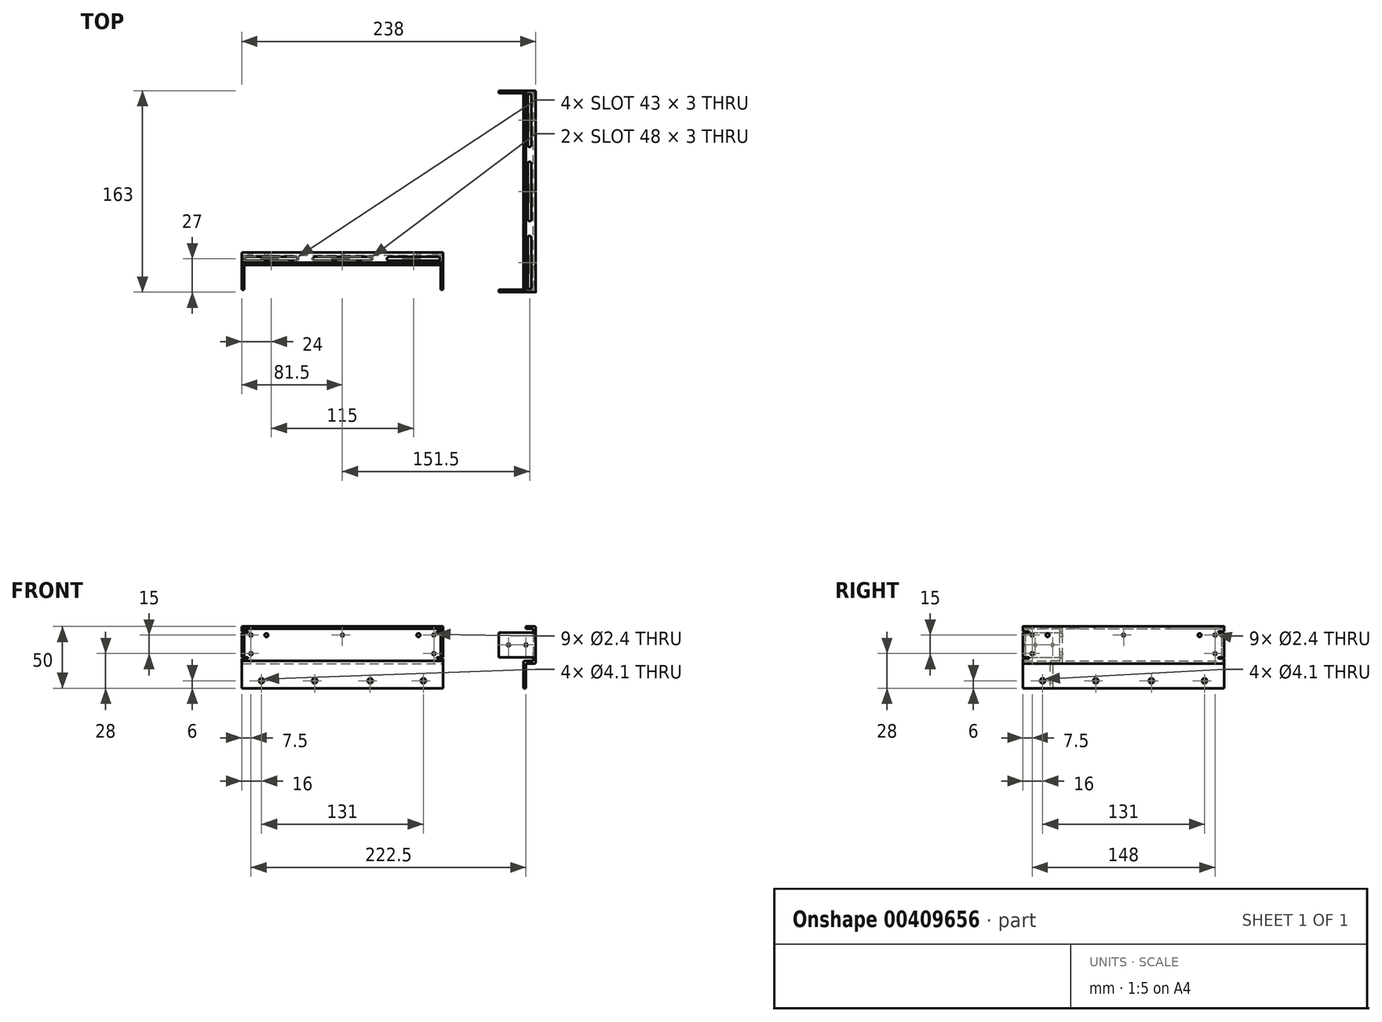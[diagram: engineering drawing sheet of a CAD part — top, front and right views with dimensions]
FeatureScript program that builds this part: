
annotation { "Feature Type Name" : "Feature", "Feature Type Description" : "" }
export const myFeature = defineFeature(function(context is Context, id is Id, definition is map)
    precondition{}
    {
        {
            var Q0;
            Q0=qCreatedBy(makeId("Front.planeOp"),FACE);
            var sketch = newSketch(context, id + "F0", { "sketchPlane" : qUnion([Q0])});
            skLineSegment(sketch, "E0", {"start": v(-20, 60) * mm, "end": v(-12, 60) * mm});
            skLineSegment(sketch, "E1", {"start": v(-12, 60) * mm, "end": v(-12, 58) * mm});
            skLineSegment(sketch, "E2", {"start": v(-12, 58) * mm, "end": v(-18, 58) * mm});
            skLineSegment(sketch, "E3", {"start": v(-18, 58) * mm, "end": v(-18, 32) * mm});
            skLineSegment(sketch, "E4", {"start": v(-20, 30) * mm, "end": v(-20, 60) * mm});
            skLineSegment(sketch, "E5.bottom", {"start": v(-18, 32) * mm, "end": v(-10, 32) * mm});
            skLineSegment(sketch, "E5.top", {"start": v(-20, 30) * mm, "end": v(-12, 30) * mm});
            skLineSegment(sketch, "E6.top", {"start": v(-10, 10) * mm, "end": v(-12, 10) * mm});
            skLineSegment(sketch, "E6.left", {"start": v(-10, 32) * mm, "end": v(-10, 10) * mm});
            skLineSegment(sketch, "E6.right", {"start": v(-12, 30) * mm, "end": v(-12, 10) * mm});
            skSolve(sketch);
        }
        {
            var Q0;
            Q0=qSketchRegion(id+"F0",true);
            extrude(context, id + "F1", {"entities" : qUnion([Q0]), "depth" : 163 * mm});
        }
        {
            var Q0;
            Q0=makeQuery(id+"F1.opExtrude","SWEPT_FACE",FACE,{"disambiguationData":[OSD([sQuery(id+"F0.wireOp",EDGE,"E3")])]});
            var sketch = newSketch(context, id + "F2", { "sketchPlane" : qUnion([Q0])});
            skLineSegment(sketch, "E7.bottom", {"start": v(0, 35) * mm, "end": v(-2, 35) * mm});
            skLineSegment(sketch, "E7.top", {"start": v(0, 55) * mm, "end": v(-2, 55) * mm});
            skLineSegment(sketch, "E7.left", {"start": v(0, 35) * mm, "end": v(0, 55) * mm});
            skLineSegment(sketch, "E7.right", {"start": v(-2, 35) * mm, "end": v(-2, 55) * mm});
            skLineSegment(sketch, "E8.bottom", {"start": v(-163, 55) * mm, "end": v(-161, 55) * mm});
            skLineSegment(sketch, "E8.top", {"start": v(-163, 35) * mm, "end": v(-161, 35) * mm});
            skLineSegment(sketch, "E8.left", {"start": v(-163, 55) * mm, "end": v(-163, 35) * mm});
            skLineSegment(sketch, "E8.right", {"start": v(-161, 55) * mm, "end": v(-161, 35) * mm});
            skSolve(sketch);
        }
        {
            var Q0;
            Q0=qSketchRegion(id+"F2",true);
            extrude(context, id + "F3", {"entities" : qUnion([Q0]), "operationType" : NewBodyOperationType.ADD, "depth" : 28 * mm});
        }
        {
            var Q0;
            Q0=makeQuery(id+"F1.opExtrude","SWEPT_FACE",FACE,{"disambiguationData":[OSD([sQuery(id+"F0.wireOp",EDGE,"E0")])]});
            var sketch = newSketch(context, id + "F4", { "sketchPlane" : qUnion([Q0])});
            skLineSegment(sketch, "E9", {"start": v(30.39, -75) * mm, "end": v(87.94, -75) * mm, "construction": true});
            skLineSegment(sketch, "E10", {"start": v(27.83, -140) * mm, "end": v(81.96, -140) * mm, "construction": true});
            skLineSegment(sketch, "E11", {"start": v(28.86, -163) * mm, "end": v(81.02, -163) * mm, "construction": true});
            skPoint(sketch, "E12", {"position": v(-41.07, -12.5) * mm});
            skPoint(sketch, "E13", {"position": v(-41.07, -62.5) * mm});
            skPoint(sketch, "E14", {"position": v(-41.07, -87.5) * mm});
            skPoint(sketch, "E15", {"position": v(-41.07, -127.5) * mm});
            skPoint(sketch, "E16", {"position": v(-41.07, -145) * mm});
            skPoint(sketch, "E17", {"position": v(-41.07, -158) * mm});
            skLineSegment(sketch, "E18", {"start": v(-168.81, -81.5) * mm, "end": v(221.3, -81.5) * mm, "construction": true});
            skLineSegment(sketch, "E19.bottom", {"start": v(-13.5, -104) * mm, "end": v(-16.5, -104) * mm, "construction": true});
            skLineSegment(sketch, "E19.top", {"start": v(-13.5, -59) * mm, "end": v(-16.5, -59) * mm, "construction": true});
            skLineSegment(sketch, "E19.left", {"start": v(-13.5, -104) * mm, "end": v(-13.5, -59) * mm});
            skLineSegment(sketch, "E19.right", {"start": v(-16.5, -104) * mm, "end": v(-16.5, -59) * mm});
            skPoint(sketch, "E19.middle", {"position": v(-15, -81.5) * mm});
            skArc(sketch, "E20", {"start": v(-13.5, -59) * mm, "mid": v(-15, -57.5) * mm, "end": v(-16.5, -59) * mm});
            skArc(sketch, "E21", {"start": v(-16.5, -104) * mm, "mid": v(-15, -105.5) * mm, "end": v(-13.5, -104) * mm});
            skLineSegment(sketch, "E22.bottom", {"start": v(-13.5, -44) * mm, "end": v(-16.5, -44) * mm, "construction": true});
            skLineSegment(sketch, "E22.top", {"start": v(-13.5, -4) * mm, "end": v(-16.5, -4) * mm, "construction": true});
            skLineSegment(sketch, "E22.left", {"start": v(-13.5, -44) * mm, "end": v(-13.5, -4) * mm});
            skLineSegment(sketch, "E22.right", {"start": v(-16.5, -44) * mm, "end": v(-16.5, -4) * mm});
            skPoint(sketch, "E22.middle", {"position": v(-15, -24) * mm});
            skArc(sketch, "E23", {"start": v(-13.5, -4) * mm, "mid": v(-15, -2.5) * mm, "end": v(-16.5, -4) * mm});
            skArc(sketch, "E24", {"start": v(-16.5, -44) * mm, "mid": v(-15, -45.5) * mm, "end": v(-13.5, -44) * mm});
            skLineSegment(sketch, "E25.MirrorCS", {"start": v(-13.5, -159) * mm, "end": v(-16.5, -159) * mm, "construction": true});
            skLineSegment(sketch, "E26.MirrorCS", {"start": v(-13.5, -119) * mm, "end": v(-16.5, -119) * mm, "construction": true});
            skArc(sketch, "E27.MirrorCS", {"start": v(-16.5, -119) * mm, "mid": v(-15, -117.5) * mm, "end": v(-13.5, -119) * mm});
            skArc(sketch, "E28.MirrorCS", {"start": v(-13.5, -159) * mm, "mid": v(-15, -160.5) * mm, "end": v(-16.5, -159) * mm});
            skPoint(sketch, "E29.MirrorP", {"position": v(-15, -139) * mm});
            skLineSegment(sketch, "E30.MirrorCS", {"start": v(-13.5, -119) * mm, "end": v(-13.5, -159) * mm});
            skLineSegment(sketch, "E31.MirrorCS", {"start": v(-16.5, -119) * mm, "end": v(-16.5, -159) * mm});
            skSolve(sketch);
        }
        {
            var Q0;
            Q0=qSketchRegion(id+"F4",true);
            extrude(context, id + "F5", {"entities" : qUnion([Q0]), "operationType" : NewBodyOperationType.REMOVE, "oppositeDirection" : true, "depth" : 2 * mm});
        }
        {
            var Q0;
            Q0=makeQuery(id+"F1.opExtrude","SWEPT_FACE",FACE,{"disambiguationData":[OSD([sQuery(id+"F0.wireOp",EDGE,"E6.left")])]});
            var sketch = newSketch(context, id + "F6", { "sketchPlane" : qUnion([Q0])});
            skCircle(sketch, "E32", {"center": v(-16, 16) * mm, "radius": 2.05 * mm});
            skCircle(sketch, "E33", {"center": v(-104, 16) * mm, "radius": 2.05 * mm});
            skCircle(sketch, "E34", {"center": v(-7.5, 53) * mm, "radius": 1.2 * mm});
            skCircle(sketch, "E35.1.0.0", {"center": v(-81.5, 53) * mm, "radius": 1.2 * mm});
            skCircle(sketch, "E35.2.0.0", {"center": v(-155.5, 53) * mm, "radius": 1.2 * mm});
            skLineSegment(sketch, "E35.direction1", {"start": v(-7.5, 53) * mm, "end": v(-81.5, 53) * mm, "construction": true});
            skCircle(sketch, "E36", {"center": v(-147, 16) * mm, "radius": 2.05 * mm});
            skCircle(sketch, "E37", {"center": v(-59, 16) * mm, "radius": 2.05 * mm});
            skLineSegment(sketch, "E38", {"start": v(-2, 23.79) * mm, "end": v(-2, 13.85) * mm, "construction": true});
            skLineSegment(sketch, "E39", {"start": v(-161, 24.44) * mm, "end": v(-161, 15.87) * mm, "construction": true});
            skLineSegment(sketch, "E40.0", {"start": v(-163, 58) * mm, "end": v(-163, 55) * mm});
            skLineSegment(sketch, "E41.0", {"start": v(-163, 55) * mm, "end": v(-161, 55) * mm});
            skPoint(sketch, "E42.oppositeSnap0", {"position": v(-162, 55) * mm});
            skLineSegment(sketch, "E42.bottom", {"start": v(-163, 56) * mm, "end": v(-158, 56) * mm});
            skLineSegment(sketch, "E42.top", {"start": v(-163, 55) * mm, "end": v(-158, 55) * mm});
            skLineSegment(sketch, "E42.left", {"start": v(-163, 56) * mm, "end": v(-163, 55) * mm});
            skLineSegment(sketch, "E42.right", {"start": v(-158, 56) * mm, "end": v(-158, 55) * mm});
            skLineSegment(sketch, "E43.0", {"start": v(-163, 35) * mm, "end": v(-161, 35) * mm});
            skLineSegment(sketch, "E43.1", {"start": v(-163, 35) * mm, "end": v(-163, 32) * mm});
            skLineSegment(sketch, "E44.bottom", {"start": v(-163, 35) * mm, "end": v(-158, 35) * mm});
            skLineSegment(sketch, "E44.top", {"start": v(-163, 34) * mm, "end": v(-158, 34) * mm});
            skLineSegment(sketch, "E44.left", {"start": v(-163, 35) * mm, "end": v(-163, 34) * mm});
            skLineSegment(sketch, "E44.right", {"start": v(-158, 35) * mm, "end": v(-158, 34) * mm});
            skLineSegment(sketch, "E45.0", {"start": v(0, 58) * mm, "end": v(0, 55) * mm});
            skLineSegment(sketch, "E45.1", {"start": v(0, 55) * mm, "end": v(-2, 55) * mm});
            skLineSegment(sketch, "E45.2", {"start": v(0, 35) * mm, "end": v(-2, 35) * mm});
            skLineSegment(sketch, "E45.3", {"start": v(0, 35) * mm, "end": v(0, 32) * mm});
            skLineSegment(sketch, "E46.bottom", {"start": v(0, 55) * mm, "end": v(-5, 55) * mm});
            skLineSegment(sketch, "E46.top", {"start": v(0, 56) * mm, "end": v(-5, 56) * mm});
            skLineSegment(sketch, "E46.left", {"start": v(0, 55) * mm, "end": v(0, 56) * mm});
            skLineSegment(sketch, "E46.right", {"start": v(-5, 55) * mm, "end": v(-5, 56) * mm});
            skLineSegment(sketch, "E47.bottom", {"start": v(0, 35) * mm, "end": v(-5, 35) * mm});
            skLineSegment(sketch, "E47.top", {"start": v(0, 34) * mm, "end": v(-5, 34) * mm});
            skLineSegment(sketch, "E47.left", {"start": v(0, 35) * mm, "end": v(0, 34) * mm});
            skLineSegment(sketch, "E47.right", {"start": v(-5, 35) * mm, "end": v(-5, 34) * mm});
            skCircle(sketch, "E48", {"center": v(-7.5, 38) * mm, "radius": 1.2 * mm});
            skCircle(sketch, "E49", {"center": v(-155.5, 38) * mm, "radius": 1.2 * mm});
            skCircle(sketch, "E50", {"center": v(-20, 53) * mm, "radius": 1.5 * mm});
            skCircle(sketch, "E51", {"center": v(-143, 53) * mm, "radius": 1.5 * mm});
            skSolve(sketch);
        }
        {
            var Q0;
            Q0=qSketchRegion(id+"F6",true);
            extrude(context, id + "F7", {"entities" : qUnion([Q0]), "operationType" : NewBodyOperationType.REMOVE, "oppositeDirection" : true, "depth" : 25 * mm});
        }
        {
            var Q0;
            Q0=makeQuery(id+"F3.boolean.opBoolean","MERGE",FACE,{"derivedFrom":[makeQuery(id+"F1.opExtrude","CAP_FACE",FACE,{"disambiguationData":[OSD([sQuery(id+"F0.wireOp",EDGE,"E0"),sQuery(id+"F0.wireOp",EDGE,"E1"),sQuery(id+"F0.wireOp",EDGE,"E2"),sQuery(id+"F0.wireOp",EDGE,"E3"),sQuery(id+"F0.wireOp",EDGE,"E4"),sQuery(id+"F0.wireOp",EDGE,"E5.bottom"),sQuery(id+"F0.wireOp",EDGE,"E5.top"),sQuery(id+"F0.wireOp",EDGE,"E6.top"),sQuery(id+"F0.wireOp",EDGE,"E6.left"),sQuery(id+"F0.wireOp",EDGE,"E6.right")])],"isStart":false}),makeQuery(id+"F3.opExtrude","SWEPT_FACE",FACE,{"disambiguationData":[OSD([sQuery(id+"F2.wireOp",EDGE,"E8.left")])]})]});
            var sketch = newSketch(context, id + "F8", { "sketchPlane" : qUnion([Q0])});
            skCircle(sketch, "E52", {"center": v(-12, 45) * mm, "radius": 1.2 * mm});
            skPoint(sketch, "E53", {"position": v(10, 45) * mm});
            skCircle(sketch, "E54", {"center": v(2, 45) * mm, "radius": 1.2 * mm});
            skSolve(sketch);
        }
        {
            var Q0;
            Q0=qSketchRegion(id+"F8",true);
            extrude(context, id + "F9", {"entities" : qUnion([Q0]), "operationType" : NewBodyOperationType.REMOVE, "endBound" : BoundingType.THROUGH_ALL, "oppositeDirection" : true, "depth" : 2 * mm});
        }
        {
            var Q0;
            Q0=makeQuery(id+"F1.opExtrude","SWEPT_EDGE",EDGE,{"disambiguationData":[OSD([sQuery(id+"F0.wireOp",EDGE,"E0"),sQuery(id+"F0.wireOp",EDGE,"E4")])]});
            var Q1;
            Q1=makeQuery(id+"F1.opExtrude","SWEPT_EDGE",EDGE,{"disambiguationData":[OSD([sQuery(id+"F0.wireOp",EDGE,"E2"),sQuery(id+"F0.wireOp",EDGE,"E3")])]});
            var Q2;
            Q2=makeQuery(id+"F1.opExtrude","SWEPT_EDGE",EDGE,{"disambiguationData":[OSD([sQuery(id+"F0.wireOp",EDGE,"E3"),sQuery(id+"F0.wireOp",EDGE,"E5.bottom")])]});
            var Q3;
            Q3=makeQuery(id+"F1.opExtrude","SWEPT_EDGE",EDGE,{"disambiguationData":[OSD([sQuery(id+"F0.wireOp",EDGE,"E5.bottom"),sQuery(id+"F0.wireOp",EDGE,"E6.left")])]});
            var Q4;
            Q4=makeQuery(id+"F1.opExtrude","SWEPT_EDGE",EDGE,{"disambiguationData":[OSD([sQuery(id+"F0.wireOp",EDGE,"E4"),sQuery(id+"F0.wireOp",EDGE,"E5.top")])]});
            var Q5;
            Q5=makeQuery(id+"F1.opExtrude","SWEPT_EDGE",EDGE,{"disambiguationData":[OSD([sQuery(id+"F0.wireOp",EDGE,"E5.top"),sQuery(id+"F0.wireOp",EDGE,"E6.right")])]});
            fillet(context, id + "F10", {"entities" : qUnion([Q0, Q1, Q2, Q3, Q4, Q5]), "radius" : 1 * mm, "tangentPropagation" : true, "allowEdgeOverflow" : false});
        }
        {
            var Q0;
            Q0=makeQuery(id+"F3.opExtrude","CAP_EDGE",EDGE,{"disambiguationData":[OSD([sQuery(id+"F2.wireOp",EDGE,"E8.right")])],"isStart":true});
            var Q1;
            {var subQ0=sQuery(id+"F0.wireOp",EDGE,"E4");Q1=makeQuery(id+"F7.boolean.opBoolean","SPLIT",EDGE,{"disambiguationData":[TD([makeQuery(id+"F3.opExtrude","SWEPT_FACE",FACE,{"disambiguationData":[OSD([sQuery(id+"F2.wireOp",EDGE,"E8.bottom")])]})])],"derivedFrom":makeQuery(id+"F1.opExtrude","CAP_EDGE",EDGE,{"disambiguationData":[OSD([subQ0])],"isStart":false})});}
            var Q2;
            Q2=makeQuery(id+"F3.opExtrude","CAP_EDGE",EDGE,{"disambiguationData":[OSD([sQuery(id+"F2.wireOp",EDGE,"E7.right")])],"isStart":true});
            var Q3;
            {var subQ0=sQuery(id+"F0.wireOp",EDGE,"E4");Q3=makeQuery(id+"F7.boolean.opBoolean","SPLIT",EDGE,{"disambiguationData":[TD([makeQuery(id+"F3.opExtrude","SWEPT_FACE",FACE,{"disambiguationData":[OSD([sQuery(id+"F2.wireOp",EDGE,"E7.bottom")])]})])],"derivedFrom":makeQuery(id+"F1.opExtrude","CAP_EDGE",EDGE,{"disambiguationData":[OSD([subQ0])],"isStart":true})});}
            fillet(context, id + "F11", {"entities" : qUnion([Q0, Q1, Q2, Q3]), "radius" : 1 * mm, "tangentPropagation" : true, "allowEdgeOverflow" : false});
        }
        {
            var Q0;
            Q0=qCreatedBy(makeId("Right.planeOp"),FACE);
            cPlane(context, id + "F12", {"entities" : qUnion([Q0]), "cplaneType" : CPlaneType.OFFSET, "offset" : 113 * mm, "width" : 150 * mm, "height" : 150 * mm});
        }
        {
            var Q0;
            Q0=makeQuery(id+"F1.opExtrude","SWEPT_BODY",BODY,{"disambiguationData":[OSD([sQuery(id+"F0.wireOp",EDGE,"E0"),sQuery(id+"F0.wireOp",EDGE,"E1"),sQuery(id+"F0.wireOp",EDGE,"E2"),sQuery(id+"F0.wireOp",EDGE,"E3"),sQuery(id+"F0.wireOp",EDGE,"xb1tLthF-IiVW-rdyS-DzM4-F0JxlruL6ZiX"),sQuery(id+"F0.wireOp",EDGE,"E4")])]});
            var Q1;
            Q1=qCreatedBy(id+"F12.planeOp",FACE);
            mirror(context, id + "F13", {"entities" : qUnion([Q0]), "mirrorPlane" : qUnion([Q1])});
        }
        {
            var Q0;
            Q0=makeQuery(id+"F1.opExtrude","SWEPT_BODY",BODY,{"disambiguationData":[OSD([sQuery(id+"F0.wireOp",EDGE,"E0"),sQuery(id+"F0.wireOp",EDGE,"E1"),sQuery(id+"F0.wireOp",EDGE,"E2"),sQuery(id+"F0.wireOp",EDGE,"E3"),sQuery(id+"F0.wireOp",EDGE,"E4"),sQuery(id+"F0.wireOp",EDGE,"E5.bottom"),sQuery(id+"F0.wireOp",EDGE,"E5.top"),sQuery(id+"F0.wireOp",EDGE,"E6.top"),sQuery(id+"F0.wireOp",EDGE,"E6.left"),sQuery(id+"F0.wireOp",EDGE,"E6.right")])]});
            var Q1;
            Q1=makeQuery(id+"F3.opExtrude","CAP_EDGE",EDGE,{"disambiguationData":[OSD([sQuery(id+"F2.wireOp",EDGE,"E8.right")])],"isStart":false});
            transform(context, id + "F14", {"entities" : qUnion([Q0]), "transformType" : TransformType.ROTATION, "transformAxis" : qUnion([Q1]), "angle" : 90 * degree, "makeCopy" : false});
        }
    });
